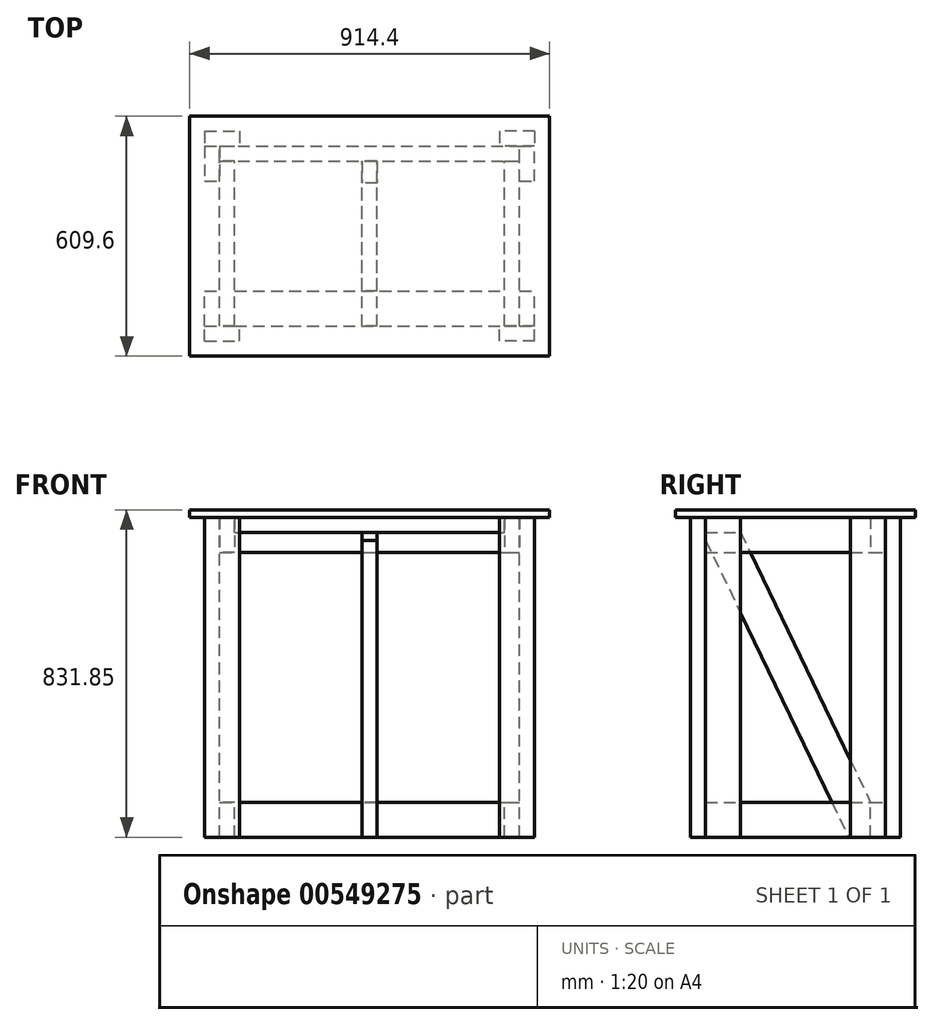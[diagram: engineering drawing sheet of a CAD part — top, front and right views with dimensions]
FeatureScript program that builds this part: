
annotation { "Feature Type Name" : "Feature", "Feature Type Description" : "" }
export const myFeature = defineFeature(function(context is Context, id is Id, definition is map)
    precondition{}
    {
        {
            var Q0;
            Q0=qCreatedBy(makeId("Top.planeOp"),FACE);
            var sketch = newSketch(context, id + "F0", { "sketchPlane" : qUnion([Q0])});
            skLineSegment(sketch, "E0.bottom", {"start": v(457.2, -304.8) * mm, "end": v(-457.2, -304.8) * mm});
            skLineSegment(sketch, "E0.top", {"start": v(457.2, 304.8) * mm, "end": v(-457.2, 304.8) * mm});
            skLineSegment(sketch, "E0.left", {"start": v(457.2, -304.8) * mm, "end": v(457.2, 304.8) * mm});
            skLineSegment(sketch, "E0.right", {"start": v(-457.2, -304.8) * mm, "end": v(-457.2, 304.8) * mm});
            skPoint(sketch, "E0.middle", {"position": v(0, 0) * mm});
            skSolve(sketch);
        }
        {
            var Q0;
            Q0 = qSketchRegion(id + "F0", true);
            extrude(context, id + "F1", {"entities" : qUnion([Q0]), "depth" : 19.05 * mm, "offsetDistance" : 25.4 * mm});
        }
        {
            var Q0;
            Q0=makeQuery(id+"F1.opExtrude","CAP_FACE",FACE,{"disambiguationData":[OSD([sQuery(id+"F0.wireOp",EDGE,"E0.bottom"),sQuery(id+"F0.wireOp",EDGE,"E0.top"),sQuery(id+"F0.wireOp",EDGE,"E0.left"),sQuery(id+"F0.wireOp",EDGE,"E0.right")])],"isStart":true});
            var sketch = newSketch(context, id + "F2", { "sketchPlane" : qUnion([Q0])});
            skLineSegment(sketch, "E1.bottom", {"start": v(-419.1, 266.7) * mm, "end": v(419.1, 266.7) * mm, "construction": true});
            skLineSegment(sketch, "E1.top", {"start": v(-419.1, -266.7) * mm, "end": v(419.1, -266.7) * mm, "construction": true});
            skLineSegment(sketch, "E1.left", {"start": v(-419.1, 266.7) * mm, "end": v(-419.1, -266.7) * mm, "construction": true});
            skLineSegment(sketch, "E1.right", {"start": v(419.1, 266.7) * mm, "end": v(419.1, -266.7) * mm, "construction": true});
            skPoint(sketch, "E1.middle", {"position": v(0, 0) * mm});
            skLineSegment(sketch, "E2.bottom", {"start": v(-419.1, 266.7) * mm, "end": v(-330.2, 266.7) * mm});
            skLineSegment(sketch, "E2.top", {"start": v(-419.1, 228.6) * mm, "end": v(-330.2, 228.6) * mm});
            skLineSegment(sketch, "E2.left", {"start": v(-419.1, 266.7) * mm, "end": v(-419.1, 228.6) * mm});
            skLineSegment(sketch, "E2.right", {"start": v(-330.2, 266.7) * mm, "end": v(-330.2, 228.6) * mm});
            skLineSegment(sketch, "E3.bottom", {"start": v(-419.1, -266.7) * mm, "end": v(-330.2, -266.7) * mm});
            skLineSegment(sketch, "E3.top", {"start": v(-419.1, -228.6) * mm, "end": v(-330.2, -228.6) * mm});
            skLineSegment(sketch, "E3.left", {"start": v(-419.1, -266.7) * mm, "end": v(-419.1, -228.6) * mm});
            skLineSegment(sketch, "E3.right", {"start": v(-330.2, -266.7) * mm, "end": v(-330.2, -228.6) * mm});
            skLineSegment(sketch, "E4.bottom", {"start": v(419.1, 266.7) * mm, "end": v(330.2, 266.7) * mm});
            skLineSegment(sketch, "E4.top", {"start": v(419.1, 228.6) * mm, "end": v(330.2, 228.6) * mm});
            skLineSegment(sketch, "E4.left", {"start": v(419.1, 266.7) * mm, "end": v(419.1, 228.6) * mm});
            skLineSegment(sketch, "E4.right", {"start": v(330.2, 266.7) * mm, "end": v(330.2, 228.6) * mm});
            skLineSegment(sketch, "E5.bottom", {"start": v(419.1, -266.7) * mm, "end": v(330.2, -266.7) * mm});
            skLineSegment(sketch, "E5.top", {"start": v(419.1, -228.6) * mm, "end": v(330.2, -228.6) * mm});
            skLineSegment(sketch, "E5.left", {"start": v(419.1, -266.7) * mm, "end": v(419.1, -228.6) * mm});
            skLineSegment(sketch, "E5.right", {"start": v(330.2, -266.7) * mm, "end": v(330.2, -228.6) * mm});
            skSolve(sketch);
        }
        {
            var Q0;
            Q0 = qSketchRegion(id + "F2", true);
            extrude(context, id + "F3", {"entities" : qUnion([Q0]), "depth" : 812.8 * mm, "offsetDistance" : 25.4 * mm});
        }
        {
            var Q0;
            Q0=makeQuery(id+"F1.opExtrude","CAP_FACE",FACE,{"disambiguationData":[OSD([sQuery(id+"F0.wireOp",EDGE,"E0.bottom"),sQuery(id+"F0.wireOp",EDGE,"E0.top"),sQuery(id+"F0.wireOp",EDGE,"E0.left"),sQuery(id+"F0.wireOp",EDGE,"E0.right")])],"isStart":true});
            var sketch = newSketch(context, id + "F4", { "sketchPlane" : qUnion([Q0])});
            skLineSegment(sketch, "E6.bottom", {"start": v(-419.1, 228.6) * mm, "end": v(-381, 228.6) * mm});
            skLineSegment(sketch, "E6.top", {"start": v(-419.1, 139.7) * mm, "end": v(-381, 139.7) * mm});
            skLineSegment(sketch, "E6.left", {"start": v(-419.1, 228.6) * mm, "end": v(-419.1, 139.7) * mm});
            skLineSegment(sketch, "E6.right", {"start": v(-381, 228.6) * mm, "end": v(-381, 139.7) * mm});
            skLineSegment(sketch, "E7.bottom", {"start": v(-419.1, -228.6) * mm, "end": v(-381, -228.6) * mm});
            skLineSegment(sketch, "E7.top", {"start": v(-419.1, -139.7) * mm, "end": v(-381, -139.7) * mm});
            skLineSegment(sketch, "E7.left", {"start": v(-419.1, -228.6) * mm, "end": v(-419.1, -139.7) * mm});
            skLineSegment(sketch, "E7.right", {"start": v(-381, -228.6) * mm, "end": v(-381, -139.7) * mm});
            skLineSegment(sketch, "E8.bottom", {"start": v(381, 228.6) * mm, "end": v(419.1, 228.6) * mm});
            skLineSegment(sketch, "E8.top", {"start": v(381, 139.7) * mm, "end": v(419.1, 139.7) * mm});
            skLineSegment(sketch, "E8.left", {"start": v(381, 228.6) * mm, "end": v(381, 139.7) * mm});
            skLineSegment(sketch, "E8.right", {"start": v(419.1, 228.6) * mm, "end": v(419.1, 139.7) * mm});
            skLineSegment(sketch, "E9.bottom", {"start": v(381, -139.7) * mm, "end": v(419.1, -139.7) * mm});
            skLineSegment(sketch, "E9.top", {"start": v(381, -228.6) * mm, "end": v(419.1, -228.6) * mm});
            skLineSegment(sketch, "E9.left", {"start": v(381, -139.7) * mm, "end": v(381, -228.6) * mm});
            skLineSegment(sketch, "E9.right", {"start": v(419.1, -139.7) * mm, "end": v(419.1, -228.6) * mm});
            skSolve(sketch);
        }
        {
            var Q0;
            Q0 = qSketchRegion(id + "F4", true);
            var Q1;
            Q1=makeQuery(id+"F3.opExtrude","CAP_FACE",FACE,{"disambiguationData":[OSD([sQuery(id+"F2.wireOp",EDGE,"E3.bottom"),sQuery(id+"F2.wireOp",EDGE,"E3.top"),sQuery(id+"F2.wireOp",EDGE,"E3.left"),sQuery(id+"F2.wireOp",EDGE,"E3.right")])],"isStart":false});
            extrude(context, id + "F5", {"entities" : qUnion([Q0]), "endBound" : BoundingType.UP_TO_SURFACE, "depth" : 25.4 * mm, "endBoundEntityFace" : qUnion([Q1]), "offsetDistance" : 25.4 * mm});
        }
        {
            var Q0;
            Q0=makeQuery(id+"F3.opExtrude","SWEPT_FACE",FACE,{"disambiguationData":[OSD([sQuery(id+"F2.wireOp",EDGE,"E3.top")])]});
            var sketch = newSketch(context, id + "F6", { "sketchPlane" : qUnion([Q0])});
            skLineSegment(sketch, "E10.bottom", {"start": v(-381, 0) * mm, "end": v(381, 0) * mm});
            skLineSegment(sketch, "E10.top", {"start": v(-381, -88.9) * mm, "end": v(381, -88.9) * mm});
            skLineSegment(sketch, "E10.left", {"start": v(-381, 0) * mm, "end": v(-381, -88.9) * mm});
            skLineSegment(sketch, "E10.right", {"start": v(381, 0) * mm, "end": v(381, -88.9) * mm});
            skLineSegment(sketch, "E11.bottom", {"start": v(-381, -812.8) * mm, "end": v(381, -812.8) * mm});
            skLineSegment(sketch, "E11.top", {"start": v(-381, -723.9) * mm, "end": v(381, -723.9) * mm});
            skLineSegment(sketch, "E11.left", {"start": v(-381, -812.8) * mm, "end": v(-381, -723.9) * mm});
            skLineSegment(sketch, "E11.right", {"start": v(381, -812.8) * mm, "end": v(381, -723.9) * mm});
            skSolve(sketch);
        }
        {
            var Q0;
            Q0 = qSketchRegion(id + "F6", true);
            extrude(context, id + "F7", {"entities" : qUnion([Q0]), "depth" : 38.1 * mm, "offsetDistance" : 25.4 * mm});
        }
        {
            var Q0;
            Q0=makeQuery(id+"F5.opExtrude","SWEPT_FACE",FACE,{"disambiguationData":[OSD([sQuery(id+"F4.wireOp",EDGE,"E7.right")])]});
            var sketch = newSketch(context, id + "F8", { "sketchPlane" : qUnion([Q0])});
            skLineSegment(sketch, "E12.bottom", {"start": v(-228.6, 0) * mm, "end": v(190.5, 0) * mm});
            skLineSegment(sketch, "E12.top", {"start": v(-228.6, -88.9) * mm, "end": v(190.5, -88.9) * mm});
            skLineSegment(sketch, "E12.left", {"start": v(-228.6, 0) * mm, "end": v(-228.6, -88.9) * mm});
            skLineSegment(sketch, "E12.right", {"start": v(190.5, 0) * mm, "end": v(190.5, -88.9) * mm});
            skLineSegment(sketch, "E13.bottom", {"start": v(-228.6, -812.8) * mm, "end": v(190.5, -812.8) * mm});
            skLineSegment(sketch, "E13.top", {"start": v(-228.6, -723.9) * mm, "end": v(190.5, -723.9) * mm});
            skLineSegment(sketch, "E13.left", {"start": v(-228.6, -812.8) * mm, "end": v(-228.6, -723.9) * mm});
            skLineSegment(sketch, "E13.right", {"start": v(190.5, -812.8) * mm, "end": v(190.5, -723.9) * mm});
            skSolve(sketch);
        }
        {
            var Q0;
            Q0 = qSketchRegion(id + "F8", true);
            extrude(context, id + "F9", {"entities" : qUnion([Q0]), "depth" : 38.1 * mm, "offsetDistance" : 25.4 * mm});
        }
        {
            var Q0;
            Q0=makeQuery(id+"F9.opExtrude","SWEPT_BODY",BODY,{"disambiguationData":[OSD([sQuery(id+"F8.wireOp",EDGE,"E12.bottom"),sQuery(id+"F8.wireOp",EDGE,"E12.top"),sQuery(id+"F8.wireOp",EDGE,"E12.left"),sQuery(id+"F8.wireOp",EDGE,"E12.right")])]});
            var Q1;
            Q1=makeQuery(id+"F9.opExtrude","SWEPT_BODY",BODY,{"disambiguationData":[OSD([sQuery(id+"F8.wireOp",EDGE,"E13.bottom"),sQuery(id+"F8.wireOp",EDGE,"E13.top"),sQuery(id+"F8.wireOp",EDGE,"E13.left"),sQuery(id+"F8.wireOp",EDGE,"E13.right")])]});
            var Q2;
            Q2=qCreatedBy(makeId("Right.planeOp"),FACE);
            mirror(context, id + "F10", {"entities" : qUnion([Q0, Q1]), "mirrorPlane" : qUnion([Q2])});
        }
        {
            var Q0;
            Q0=makeQuery(id+"F2.imprint","IMPRINT",FACE,{"disambiguationData":[TD([[makeQuery(id+"F2.imprint","IMPRINT",EDGE,{"derivedFrom":sQuery(id+"F2.wireOp",EDGE,"E2.bottom")}),1.0]])]});
            var sketch = newSketch(context, id + "F11", { "sketchPlane" : qUnion([Q0])});
            skLineSegment(sketch, "E14.bottom", {"start": v(-342.9, 228.6) * mm, "end": v(342.9, 228.6) * mm});
            skLineSegment(sketch, "E14.top", {"start": v(-342.9, 139.7) * mm, "end": v(342.9, 139.7) * mm});
            skLineSegment(sketch, "E14.left", {"start": v(-342.9, 228.6) * mm, "end": v(-342.9, 139.7) * mm});
            skLineSegment(sketch, "E14.right", {"start": v(342.9, 228.6) * mm, "end": v(342.9, 139.7) * mm});
            skSolve(sketch);
        }
        {
            var Q0;
            Q0 = qSketchRegion(id + "F11", true);
            extrude(context, id + "F12", {"entities" : qUnion([Q0]), "depth" : 38.1 * mm, "offsetDistance" : 25.4 * mm});
        }
        {
            var Q0;
            Q0=qCreatedBy(makeId("Right.planeOp"),FACE);
            var sketch = newSketch(context, id + "F13", { "sketchPlane" : qUnion([Q0])});
            skLineSegment(sketch, "E15", {"start": v(-228.6, -58.39) * mm, "end": v(134.64, -812.8) * mm});
            skLineSegment(sketch, "E16.0", {"start": v(-139.7, -38.1) * mm, "end": v(190.5, -723.9) * mm});
            skLineSegment(sketch, "E17", {"start": v(190.5, -812.8) * mm, "end": v(134.64, -812.8) * mm});
            skLineSegment(sketch, "E18", {"start": v(-228.6, -38.1) * mm, "end": v(-228.6, -58.39) * mm});
            skLineSegment(sketch, "E19", {"start": v(-228.6, -38.1) * mm, "end": v(-139.7, -38.1) * mm});
            skLineSegment(sketch, "E20", {"start": v(190.5, -723.9) * mm, "end": v(190.5, -812.8) * mm});
            skSolve(sketch);
        }
        {
            var Q0;
            Q0 = qSketchRegion(id + "F13", true);
            extrude(context, id + "F14", {"entities" : qUnion([Q0]), "endBound" : BoundingType.SYMMETRIC, "depth" : 38.1 * mm, "offsetDistance" : 25.4 * mm});
        }
    });
